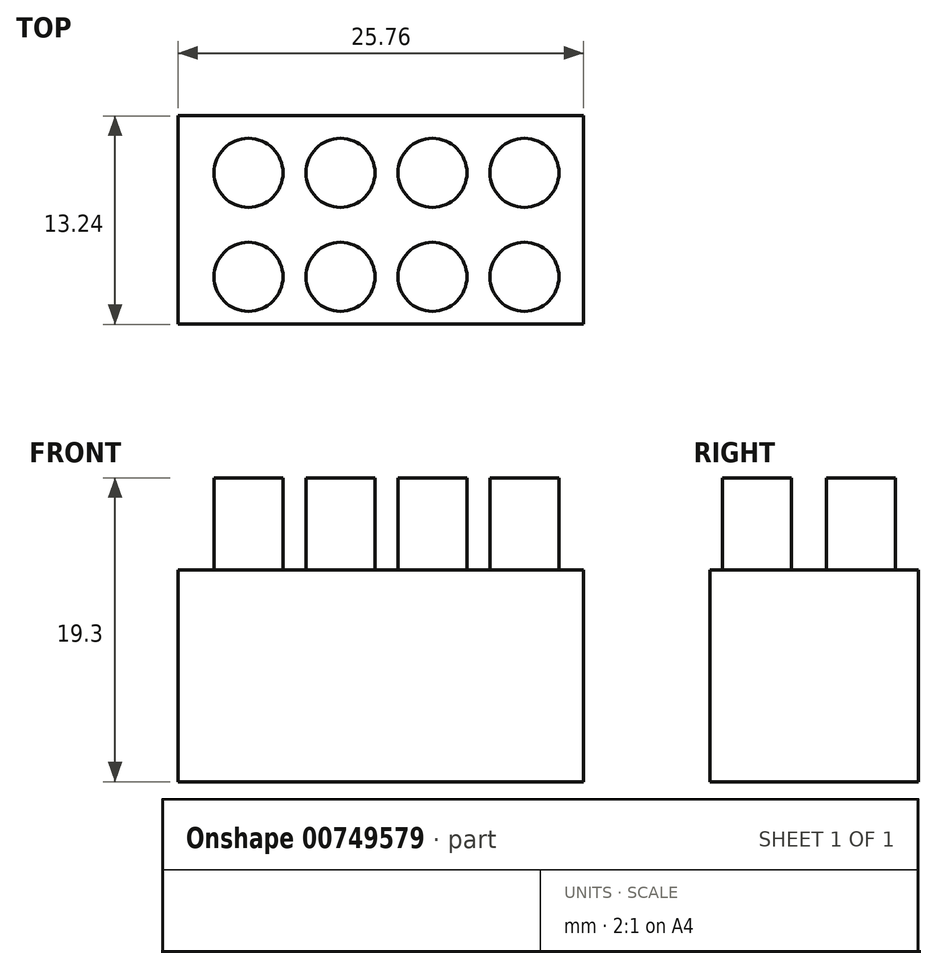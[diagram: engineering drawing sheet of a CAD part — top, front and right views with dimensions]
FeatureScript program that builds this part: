
annotation { "Feature Type Name" : "Feature", "Feature Type Description" : "" }
export const myFeature = defineFeature(function(context is Context, id is Id, definition is map)
    precondition{}
    {
        {
            var Q0;
            Q0=qCreatedBy(makeId("Top.planeOp"),FACE);
            var sketch = newSketch(context, id + "F0", { "sketchPlane" : qUnion([Q0])});
            skLineSegment(sketch, "E0.bottom", {"start": v(-60.2, 52.81) * mm, "end": v(-34.45, 52.81) * mm});
            skLineSegment(sketch, "E0.top", {"start": v(-60.2, 39.57) * mm, "end": v(-34.45, 39.57) * mm});
            skLineSegment(sketch, "E0.left", {"start": v(-60.2, 52.81) * mm, "end": v(-60.2, 39.57) * mm});
            skLineSegment(sketch, "E0.right", {"start": v(-34.45, 52.81) * mm, "end": v(-34.45, 39.57) * mm});
            skSolve(sketch);
        }
        {
            var Q0;
            Q0 = qSketchRegion(id + "F0", true);
            extrude(context, id + "F1", {"entities" : qUnion([Q0]), "depth" : 13.46 * mm, "offsetDistance" : 25.4 * mm});
        }
        {
            var Q0;
            Q0=makeQuery(id+"F1.opExtrude","CAP_FACE",FACE,{"disambiguationData":[OSD([sQuery(id+"F0.wireOp",EDGE,"E0.bottom"),sQuery(id+"F0.wireOp",EDGE,"E0.top"),sQuery(id+"F0.wireOp",EDGE,"E0.left"),sQuery(id+"F0.wireOp",EDGE,"E0.right")])],"isStart":false});
            var sketch = newSketch(context, id + "F2", { "sketchPlane" : qUnion([Q0])});
            skCircle(sketch, "E1", {"center": v(-55.74, 49.2) * mm, "radius": 2.2 * mm});
            skCircle(sketch, "E2.0.1.0", {"center": v(-55.74, 42.59) * mm, "radius": 2.2 * mm});
            skCircle(sketch, "E2.1.0.0", {"center": v(-49.9, 49.2) * mm, "radius": 2.2 * mm});
            skCircle(sketch, "E2.1.1.0", {"center": v(-49.9, 42.59) * mm, "radius": 2.2 * mm});
            skCircle(sketch, "E2.2.0.0", {"center": v(-44.06, 49.2) * mm, "radius": 2.2 * mm});
            skCircle(sketch, "E2.2.1.0", {"center": v(-44.06, 42.59) * mm, "radius": 2.2 * mm});
            skCircle(sketch, "E2.3.0.0", {"center": v(-38.21, 49.2) * mm, "radius": 2.2 * mm});
            skCircle(sketch, "E2.3.1.0", {"center": v(-38.21, 42.59) * mm, "radius": 2.2 * mm});
            skLineSegment(sketch, "E2.direction1", {"start": v(-55.74, 49.2) * mm, "end": v(-49.9, 49.2) * mm, "construction": true});
            skLineSegment(sketch, "E2.direction2", {"start": v(-55.74, 49.2) * mm, "end": v(-55.74, 42.59) * mm, "construction": true});
            skSolve(sketch);
        }
        {
            var Q0;
            Q0 = qSketchRegion(id + "F2", true);
            extrude(context, id + "F3", {"entities" : qUnion([Q0]), "operationType" : NewBodyOperationType.ADD, "depth" : 5.84 * mm, "offsetDistance" : 25.4 * mm});
        }
    });
